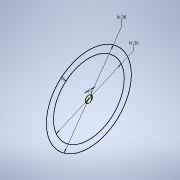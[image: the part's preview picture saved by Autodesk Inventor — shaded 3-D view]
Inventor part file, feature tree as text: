
AUTODESK INVENTOR PART (.ipt)
format: ipt  version: 2020 (Build 240168000, 168)  size: 94,720 bytes
history: native  units: in
note: dims shown in document units (in); Inventor stores cm internally (conversion verified against a paired STEP export)
features: sketch x1
ambient origin geometry x8: Origin, YZ Plane, XZ Plane, XY Plane, X Axis, Y Axis, Z Axis, Center Point
feature tree (1):
  sketch  "Sketch1"  dims[d0=0.1181in d1=0.0394in d3=1.4173in d4=0.1181in d6=1.1811in]
